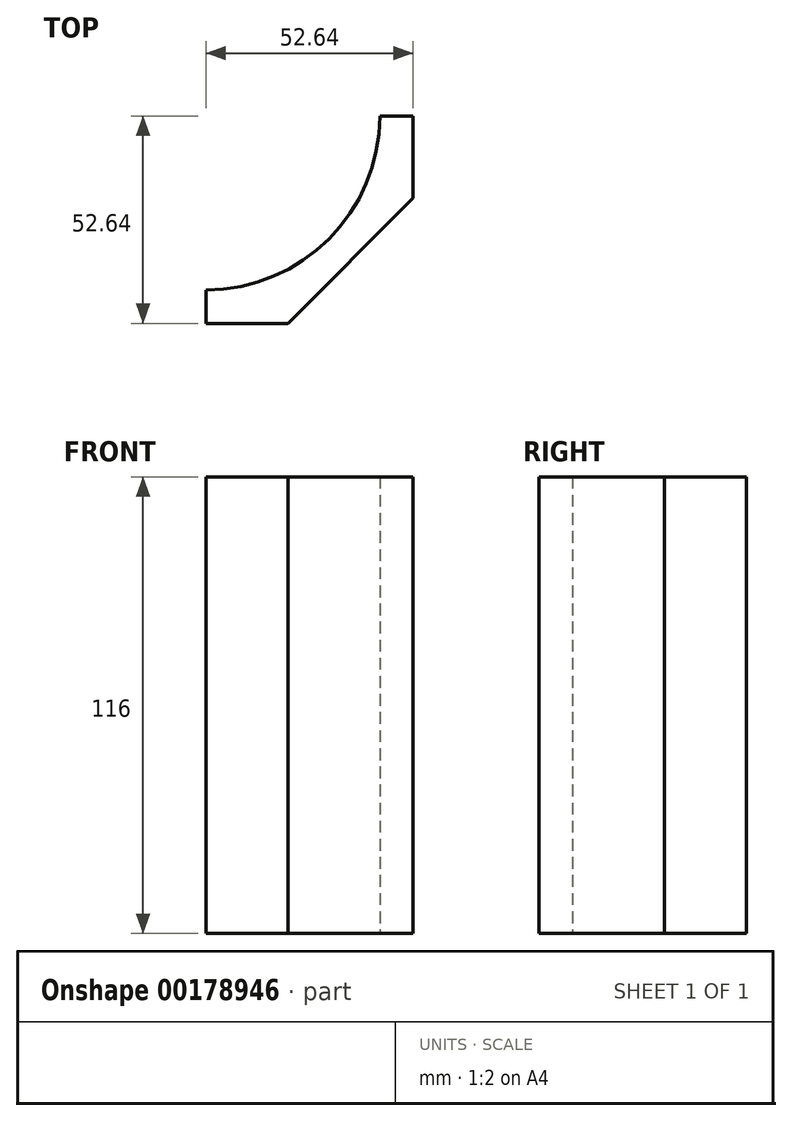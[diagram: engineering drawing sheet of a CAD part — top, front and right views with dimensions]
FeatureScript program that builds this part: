
annotation { "Feature Type Name" : "Feature", "Feature Type Description" : "" }
export const myFeature = defineFeature(function(context is Context, id is Id, definition is map)
    precondition{}
    {
        {
            var Q0;
            Q0=qCreatedBy(makeId("Top.planeOp"),FACE);
            var sketch = newSketch(context, id + "F0", { "sketchPlane" : qUnion([Q0])});
            skLineSegment(sketch, "E0", {"start": v(0, 0) * mm, "end": v(20.83, 0) * mm});
            skLineSegment(sketch, "E1", {"start": v(20.83, 0) * mm, "end": v(52.64, 31.8) * mm});
            skLineSegment(sketch, "E2", {"start": v(52.64, 31.8) * mm, "end": v(52.64, 52.64) * mm});
            skLineSegment(sketch, "E3", {"start": v(0, 0) * mm, "end": v(0, 8.47) * mm});
            skLineSegment(sketch, "E4", {"start": v(52.64, 52.64) * mm, "end": v(44.17, 52.64) * mm});
            skArc(sketch, "E5", {"start": v(0, 8.47) * mm, "mid": v(31.23, 21.4) * mm, "end": v(44.17, 52.64) * mm});
            skSolve(sketch);
        }
        {
            var Q0;
            Q0=makeQuery(id+"F0.imprint","IMPRINT",FACE,{"disambiguationData":[TD([[makeQuery(id+"F0.imprint","IMPRINT",EDGE,{"derivedFrom":sQuery(id+"F0.wireOp",EDGE,"E0")}),1.0]])]});
            extrude(context, id + "F1", {"entities" : qUnion([Q0]), "depth" : 116 * mm});
        }
    });
